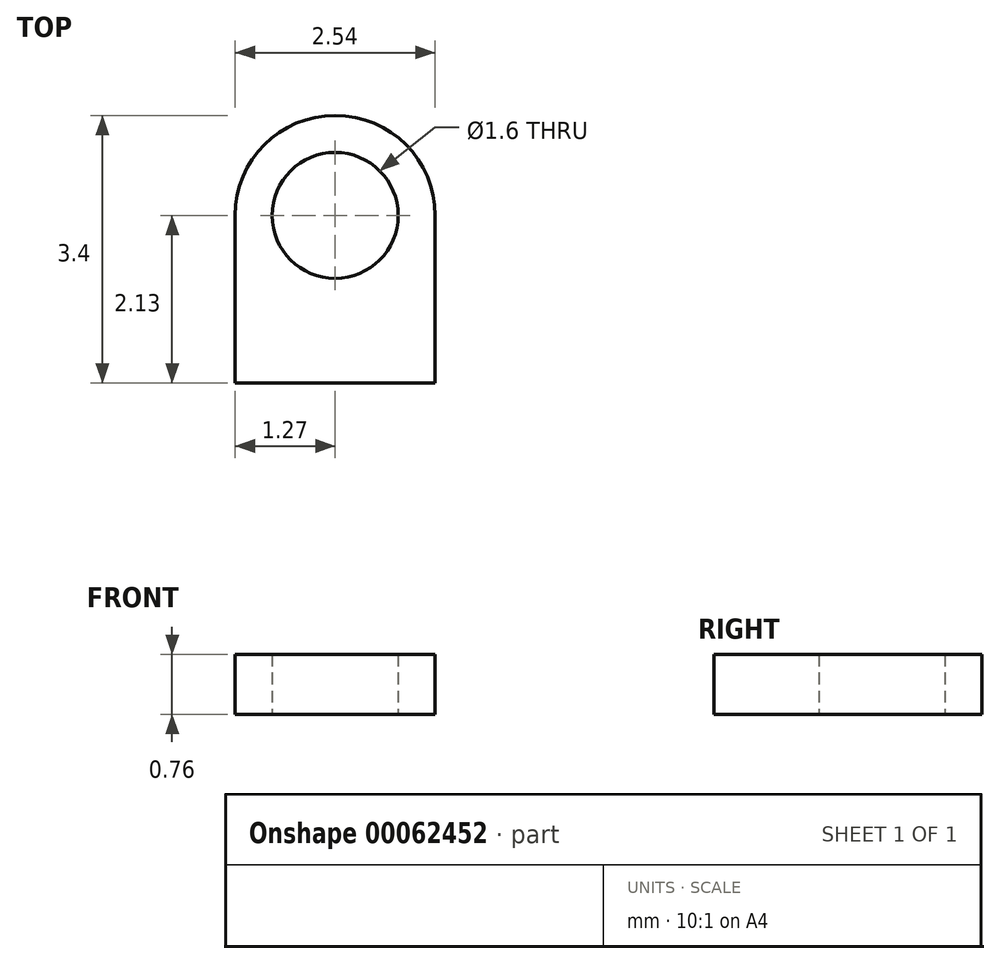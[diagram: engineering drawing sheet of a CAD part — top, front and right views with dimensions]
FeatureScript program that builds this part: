
annotation { "Feature Type Name" : "Feature", "Feature Type Description" : "" }
export const myFeature = defineFeature(function(context is Context, id is Id, definition is map)
    precondition{}
    {
        {
            var Q0;
            Q0=qCreatedBy(makeId("Top.planeOp"),FACE);
            var sketch = newSketch(context, id + "F0", { "sketchPlane" : qUnion([Q0])});
            skCircle(sketch, "E0", {"center": v(0, 0) * mm, "radius": 0.8 * mm});
            skArc(sketch, "E1", {"start": v(1.27, 0) * mm, "mid": v(0, 1.27) * mm, "end": v(-1.27, 0) * mm});
            skLineSegment(sketch, "E2", {"start": v(-1.27, 0) * mm, "end": v(-1.27, -2.13) * mm});
            skLineSegment(sketch, "E3", {"start": v(-1.27, -2.13) * mm, "end": v(1.27, -2.13) * mm});
            skLineSegment(sketch, "E4", {"start": v(1.27, -2.13) * mm, "end": v(1.27, 0) * mm});
            skSolve(sketch);
        }
        {
            var Q0;
            Q0=makeQuery(id+"F0.imprint","IMPRINT",FACE,{"disambiguationData":[TD([[makeQuery(id+"F0.imprint","IMPRINT",EDGE,{"derivedFrom":sQuery(id+"F0.wireOp",EDGE,"E0")}),-1.0]])]});
            extrude(context, id + "F1", {"entities" : qUnion([Q0]), "depth" : 0.76 * mm});
        }
    });
